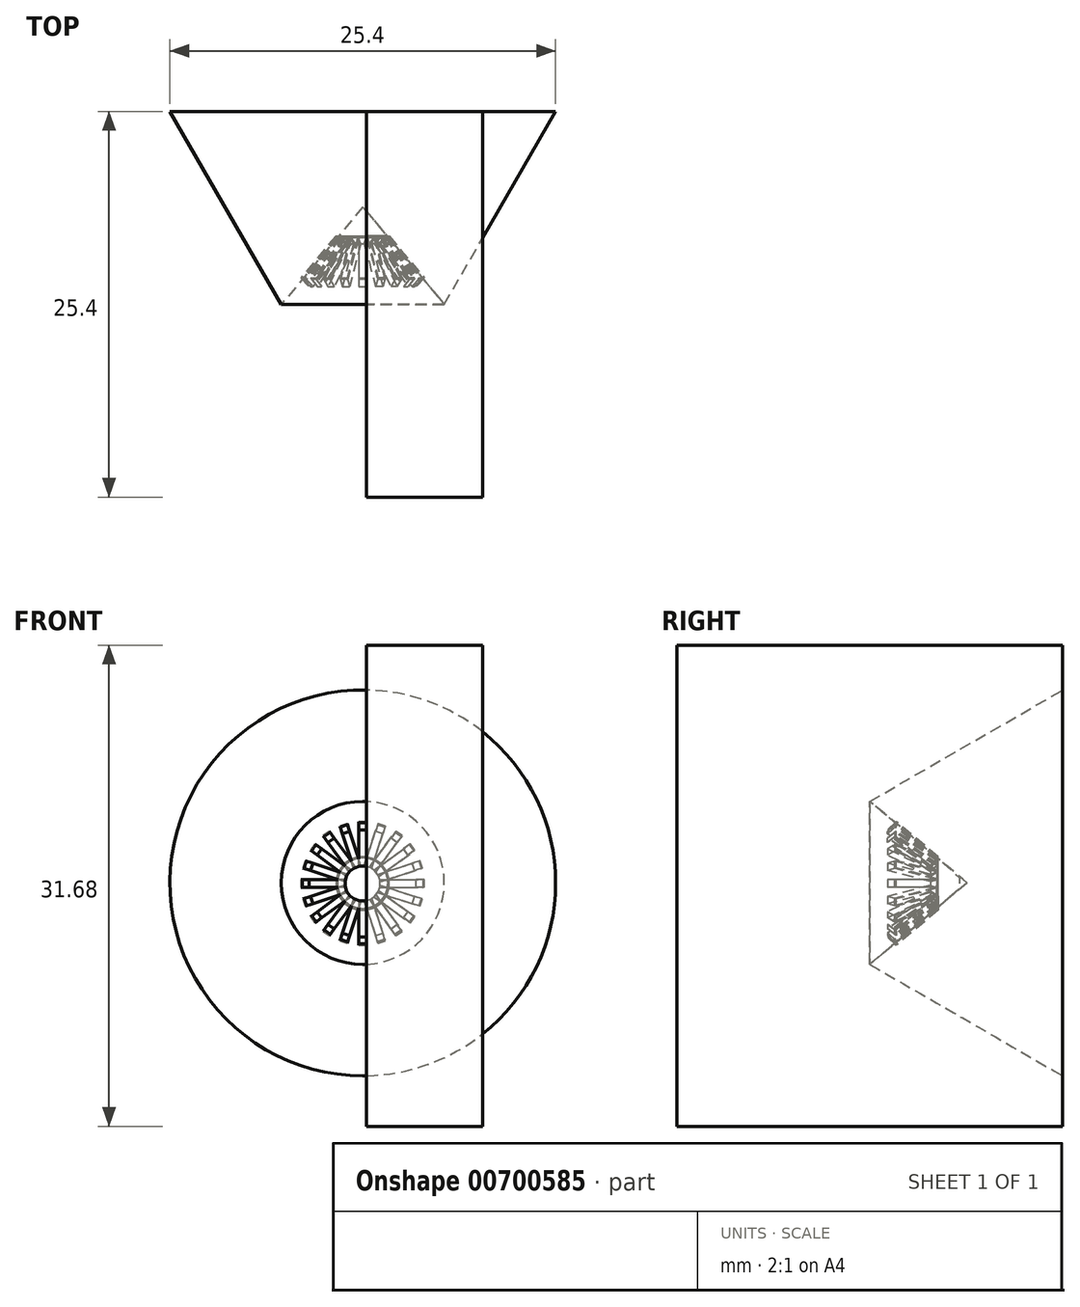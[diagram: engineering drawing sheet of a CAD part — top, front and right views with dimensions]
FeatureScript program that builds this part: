
annotation { "Feature Type Name" : "Feature", "Feature Type Description" : "" }
export const myFeature = defineFeature(function(context is Context, id is Id, definition is map)
    precondition{}
    {
        {
            var Q0;
            Q0=qCreatedBy(makeId("Front.planeOp"),FACE);
            var sketch = newSketch(context, id + "F0", { "sketchPlane" : qUnion([Q0])});
            skLineSegment(sketch, "E0", {"start": v(0, 51.45) * mm, "end": v(0, -50.15) * mm, "construction": true});
            skLineSegment(sketch, "E1", {"start": v(12.71, 0.04) * mm, "end": v(-12.69, 0.04) * mm});
            skCircle(sketch, "E2", {"center": v(0.01, 0.04) * mm, "radius": 12.7 * mm});
            skCircle(sketch, "E3", {"center": v(0.01, 0.04) * mm, "radius": 10.16 * mm});
            skSolve(sketch);
        }
        {
            var Q0;
            Q0 = qSketchRegion(id + "F0", true);
            var Q1;
            {var subQ0=sQuery(id+"F0.wireOp",EDGE,"E3");var subQ1=sQuery(id+"F0.wireOp",EDGE,"E1");var subQ2=makeQuery(id+"F0.imprint","INTERSECT",VERTEX,{"disambiguationData":[OD(0.0)],"derivedFrom":[subQ1,subQ0]});Q1=makeQuery(id+"F0.imprint","IMPRINT",FACE,{"disambiguationData":[TD([[makeQuery(id+"F0.imprint","IMPRINT",EDGE,{"disambiguationData":[TD([[subQ2,-1.0]])],"derivedFrom":subQ1}),-1.0]])]});}
            var Q2;
            {var subQ0=sQuery(id+"F0.wireOp",EDGE,"E3");var subQ1=sQuery(id+"F0.wireOp",EDGE,"E1");var subQ2=makeQuery(id+"F0.imprint","INTERSECT",VERTEX,{"disambiguationData":[OD(0.0)],"derivedFrom":[subQ1,subQ0]});Q2=makeQuery(id+"F0.imprint","IMPRINT",FACE,{"disambiguationData":[TD([[makeQuery(id+"F0.imprint","IMPRINT",EDGE,{"disambiguationData":[TD([[subQ2,-1.0]])],"derivedFrom":subQ1}),1.0]])]});}
            extrude(context, id + "F1", {"entities" : qUnion([Q0, Q1, Q2]), "depth" : 12.7 * mm, "offsetDistance" : 25.4 * mm, "hasDraft" : true, "draftAngle" : 30 * degree, "draftPullDirection" : true});
        }
        {
            var Q0;
            Q0=makeQuery(id+"F1.opExtrude","CAP_FACE",FACE,{"disambiguationData":[OSD([sQuery(id+"F0.wireOp",EDGE,"E2")])],"isStart":false});
            extrude(context, id + "F2", {"entities" : qUnion([Q0]), "operationType" : NewBodyOperationType.REMOVE, "oppositeDirection" : true, "depth" : 7.62 * mm, "offsetDistance" : 25.4 * mm, "hasDraft" : true, "draftAngle" : 40 * degree, "draftPullDirection" : true});
        }
        {
            var Q0;
            Q0=qCreatedBy(makeId("Front.planeOp"),FACE);
            var sketch = newSketch(context, id + "F3", { "sketchPlane" : qUnion([Q0])});
            skLineSegment(sketch, "E4.bottom", {"start": v(0.25, 15.7) * mm, "end": v(7.9, 15.7) * mm});
            skLineSegment(sketch, "E4.top", {"start": v(0.25, -15.99) * mm, "end": v(7.9, -15.99) * mm});
            skLineSegment(sketch, "E4.left", {"start": v(0.25, 15.7) * mm, "end": v(0.25, -15.99) * mm});
            skLineSegment(sketch, "E4.right", {"start": v(7.9, 15.7) * mm, "end": v(7.9, -15.99) * mm});
            skSolve(sketch);
        }
        {
            var Q0;
            Q0 = qSketchRegion(id + "F3", true);
            extrude(context, id + "F4", {"entities" : qUnion([Q0]), "depth" : 25.4 * mm, "offsetDistance" : 25.4 * mm});
        }
        {
            var Q0;
            Q0=makeQuery(id+"F4.opExtrude","SWEPT_FACE",FACE,{"disambiguationData":[OSD([sQuery(id+"F3.wireOp",EDGE,"E4.left")])]});
            var sketch = newSketch(context, id + "F5", { "sketchPlane" : qUnion([Q0])});
            skLineSegment(sketch, "E5", {"start": v(8.72, -1.14) * mm, "end": v(11.54, -3.51) * mm});
            skLineSegment(sketch, "E6", {"start": v(8.72, -1.14) * mm, "end": v(8.2, -1.75) * mm});
            skLineSegment(sketch, "E7", {"start": v(8.2, -1.75) * mm, "end": v(10.95, -4.06) * mm});
            skLineSegment(sketch, "E8", {"start": v(10.95, -4.06) * mm, "end": v(11.54, -3.51) * mm});
            skSolve(sketch);
        }
        {
            var Q0;
            Q0 = qSketchRegion(id + "F5", true);
            extrude(context, id + "F6", {"entities" : qUnion([Q0]), "depth" : 0.5 * mm, "offsetDistance" : 25.4 * mm});
        }
        {
            var Q0;
            Q0=qCreatedBy(makeId("Right.planeOp"),FACE);
            var sketch = newSketch(context, id + "F7", { "sketchPlane" : qUnion([Q0])});
            skLineSegment(sketch, "E9", {"start": v(0, 0) * mm, "end": v(-21.25, 0) * mm});
            skSolve(sketch);
        }
        {
            var Q0;
            Q0=makeQuery(id+"F6.opExtrude","SWEPT_BODY",BODY,{"disambiguationData":[OSD([sQuery(id+"F5.wireOp",EDGE,"E5"),sQuery(id+"F5.wireOp",EDGE,"E6"),sQuery(id+"F5.wireOp",EDGE,"E7"),sQuery(id+"F5.wireOp",EDGE,"E8")])]});
            var Q1;
            Q1=sQuery(id+"F7.wireOp",EDGE,"E9");
            circularPattern(context, id + "F8", {"entities" : qUnion([Q0]), "axis" : qUnion([Q1]), "angle" : 360 * degree, "instanceCount" : 20, "equalSpace" : true});
        }
    });
